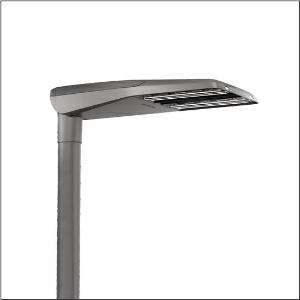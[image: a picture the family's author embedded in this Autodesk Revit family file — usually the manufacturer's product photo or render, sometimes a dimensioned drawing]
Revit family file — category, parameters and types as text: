
# Revit family: streetlight_sl_11_iq_midi___pc-r_5xc3f41f08me_b4e0
name_source: partatom
category: Lighting Fixtures
units: mm (PartAtom-declared; Revit-internal decimal feet)

## family parameters
Cut with Voids When Loaded = No
Host = Face
Light Source = No
Part Type = Normal
Room Calculation Point = No
Round Connector Dimension = Use Diameter
Shared = No

## types (1)
- --- (1 x LED, 16220 lm, 124.7 W, 4000K)
    Apparent Load = 125 VA
    CIE Flux Codes = 37 73 96 100 100
    Color Rendering = 70
    Color Temperature = 4000K
    Default Elevation = 1800 mm
    Description = Streetlight SL 11 iQ midi, mast luminaire, primary light control with 3 zone facetted reflector, of plastic, silver coated, highly specular, primary optical cover: cover, of PMMA, transparent, light distribution: PC-R, light emission: direct distribution, primary light characteristic: asymmetric, right, installation type: post-top, side-entry, LED, High Power LED, rated luminous flux: 16.220lm, luminous efficacy: 130lm/W, light colour: 740, colour temperature: 4000K, control: Street-Remote, optimised constant luminous flux control (CLO 2.0), Desk-Remote (wireless, voltage-free reading and setting of iQ features in the workshop via application-optimized NFC function/RFID function), Light-Fading, Smart-Wire, Night-Set, Lumen-Switch, Temp-Guard, Auto-Match, with cable H07RN-F 5x 1.5mm², mains connection: 230..240V, AC, 50/60Hz, connection cable pre-assembled, cable length: 12,5m, start of lifetime: 125W, end of service life: 132W, reduction: 57W, luminaire housing, of diecast aluminium, powder-coated, Siteco® metallic grey (DB 702S), please order mast flange separately, inclination adjustable without tools: 0°, 5°, 10°, 15° (post-top) | 0°, -5°, -10°, -15° (side-entry), sealing non-destructively replaceable, multi-level sealing system, length: 780mm, width: 376mm, height: 118mm, mast flange for spigot size: 42mm (side-entry): 5XC10008XM4, 60/48mm (side-entry/post-top): 5XC10108XM2, 76/60mm (side-entry/post-top): 5XC10108XM1, equipment: Power, protection rating (complete): IP66, insulation class (complete): insulation class II (safety insulation), certification: CE, ENEC, VDE, impact resistance: IK09, permissible operating ambient temperature for outdoor applications: -25..+50°C, standard-compliant lighting for roads and squares, Environmental Product Declaration (EPD) tested and certified by an independent institute, packaging unit: 1 piece

Light Distribution: PC-R
    Height = 118 mm
    Lamp = 1 x LED
    Lamp Light Flux = 16220 lm
    Lamp Power = 124.7 W
    Lamp count = 1
    Length = 780 mm
    Luminous efficacy = 130 lm/W
    Manufacturer = Siteco
    ModVariant = No
    Model = 5XC3F41F08ME
    Number of Poles = 1
    OnlyDefault = Yes
    Power Factor = 1
    Product Name = Streetlight SL 11 iQ midi | PC-R
    Product group = mast luminaire | pylon top
    ProductGroupID = 6100
    Protection Class = Protection class II
    Protection Degree = IP 66
    RLX_Detail_Level = 1
    RLX_Emergency_Light_Flux = 0 lm
    RLX_Emergency_Type = 0
    RLX_Emergency_Type_DB = No
    RlxData = <blob elided: 74525 chars, md5=81e2f9e2>
    Socket = socket
    Standby Power = 0 W
    System Light Flux = 16220 lm
    System Power = 125 W
    Type Comments = factory setting: luminous flux: 100 % | dim-lin: 254 | 557 mA
    Type Image = l_1005960.jpg
    URL = http://relux.com
    VarID = @adj_131081
    Voltage = 0 V
    Weight = 0.00 kg
    Width = 376 mm

## geometry (parser evidence)
native form markers: Blend x4, Sweep x11
no freeform markers — native parametric forms only
